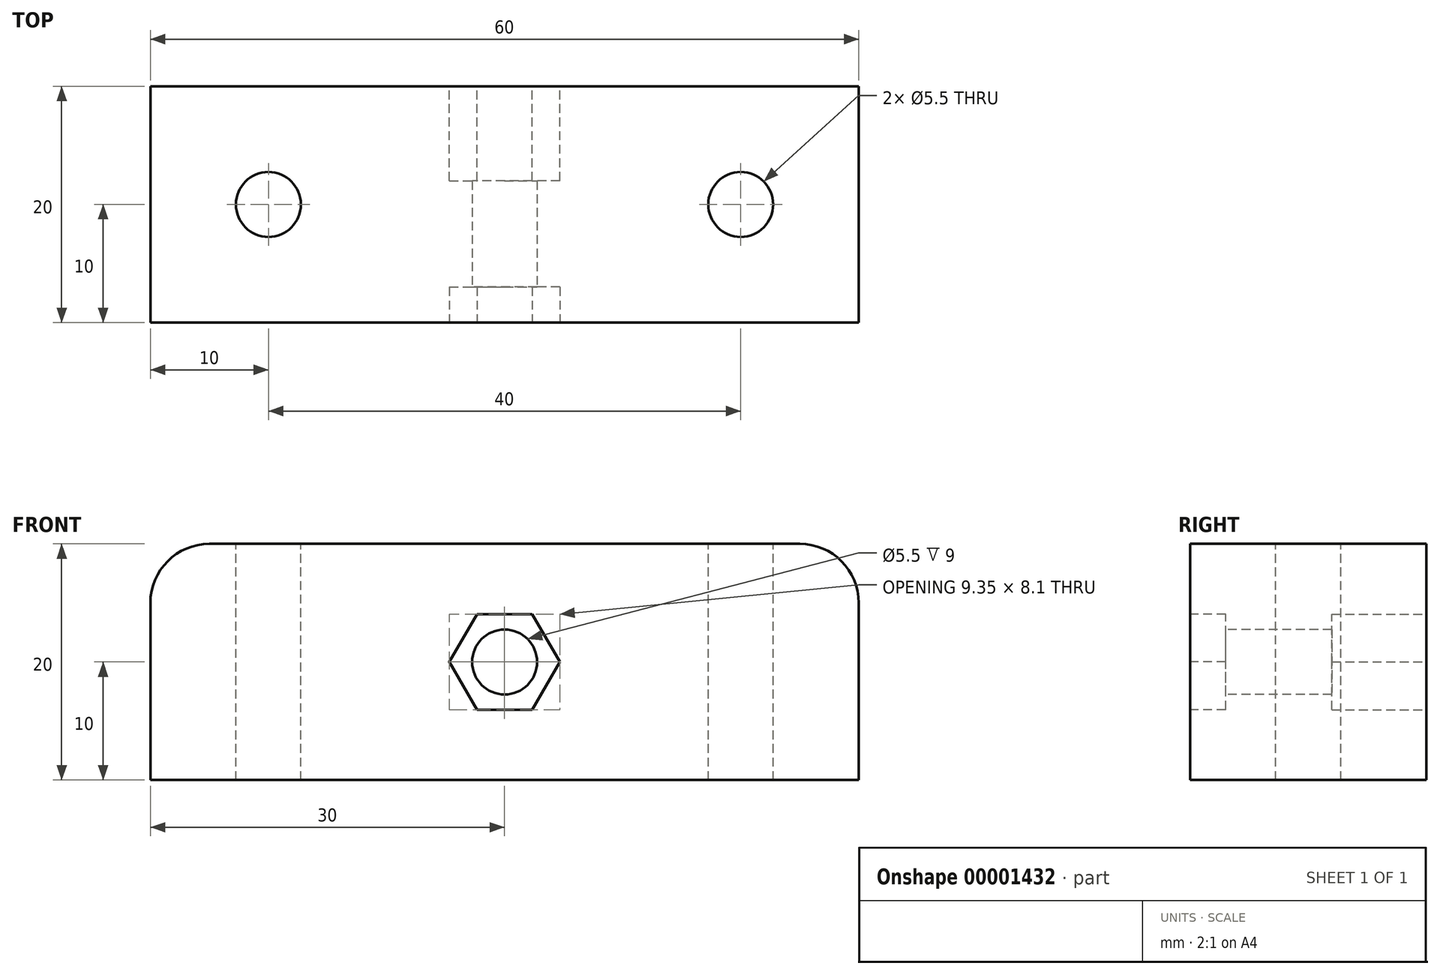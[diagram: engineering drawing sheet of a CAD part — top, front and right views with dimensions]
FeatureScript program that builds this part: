
annotation { "Feature Type Name" : "Feature", "Feature Type Description" : "" }
export const myFeature = defineFeature(function(context is Context, id is Id, definition is map)
    precondition{}
    {
        {
            var Q0;
            Q0=qCreatedBy(makeId("Top.planeOp"),FACE);
            var sketch = newSketch(context, id + "F0", { "sketchPlane" : qUnion([Q0])});
            skLineSegment(sketch, "E0.rect.bottom", {"start": v(30, 10) * mm, "end": v(-30, 10) * mm});
            skLineSegment(sketch, "E0.rect.top", {"start": v(30, -10) * mm, "end": v(-30, -10) * mm});
            skLineSegment(sketch, "E0.rect.left", {"start": v(30, 10) * mm, "end": v(30, -10) * mm});
            skLineSegment(sketch, "E0.rect.right", {"start": v(-30, 10) * mm, "end": v(-30, -10) * mm});
            skPoint(sketch, "E0.rect.middle", {"position": v(0, 0) * mm});
            skSolve(sketch);
        }
        {
            var Q0;
            Q0=makeQuery(id+"F0.imprint","IMPRINT",FACE,{"disambiguationData":[TD([[makeQuery(id+"F0.imprint","IMPRINT",EDGE,{"derivedFrom":sQuery(id+"F0.wireOp",EDGE,"E0.rect.bottom")}),1.0]])]});
            extrude(context, id + "F1", {"entities" : qUnion([Q0]), "depth" : 20 * mm});
        }
        {
            var Q0;
            Q0=makeQuery(id+"F1.opExtrude","SWEPT_FACE",FACE,{"disambiguationData":[OSD([sQuery(id+"F0.wireOp",EDGE,"E0.rect.top")])]});
            var sketch = newSketch(context, id + "F2", { "sketchPlane" : qUnion([Q0])});
            skLineSegment(sketch, "E1", {"start": v(0, 0) * mm, "end": v(0, 20) * mm, "construction": true});
            skCircle(sketch, "E2", {"center": v(0, 10) * mm, "radius": 2.75 * mm});
            skSolve(sketch);
        }
        {
            var Q0;
            Q0=makeQuery(id+"F2.imprint","IMPRINT",FACE,{"disambiguationData":[TD([[makeQuery(id+"F2.imprint","IMPRINT",EDGE,{"derivedFrom":sQuery(id+"F2.wireOp",EDGE,"E2")}),1.0]])]});
            extrude(context, id + "F3", {"entities" : qUnion([Q0]), "operationType" : NewBodyOperationType.REMOVE, "endBound" : BoundingType.THROUGH_ALL, "oppositeDirection" : true, "depth" : 25 * mm});
        }
        {
            var Q0;
            Q0=makeQuery(id+"F1.opExtrude","SWEPT_FACE",FACE,{"disambiguationData":[OSD([sQuery(id+"F0.wireOp",EDGE,"E0.rect.top")])]});
            var sketch = newSketch(context, id + "F4", { "sketchPlane" : qUnion([Q0])});
            skCircle(sketch, "E3.cCircle", {"center": v(0, 10) * mm, "radius": 4.05 * mm, "construction": true});
            skLineSegment(sketch, "E3.0", {"start": v(-2.34, 14.05) * mm, "end": v(2.34, 14.05) * mm});
            skLineSegment(sketch, "E3.1", {"start": v(2.34, 14.05) * mm, "end": v(4.68, 10) * mm});
            skLineSegment(sketch, "E3.2", {"start": v(4.68, 10) * mm, "end": v(2.34, 5.95) * mm});
            skLineSegment(sketch, "E3.3", {"start": v(2.34, 5.95) * mm, "end": v(-2.34, 5.95) * mm});
            skLineSegment(sketch, "E3.4", {"start": v(-2.34, 5.95) * mm, "end": v(-4.68, 10) * mm});
            skLineSegment(sketch, "E3.5", {"start": v(-4.68, 10) * mm, "end": v(-2.34, 14.05) * mm});
            skPoint(sketch, "E3.0.midPoint", {"position": v(0, 14.05) * mm});
            skSolve(sketch);
        }
        {
            var Q0;
            {var subQ0=makeQuery(id+"F4.imprint","IMPRINT",EDGE,{"derivedFrom":makeQuery(id+"F3.boolean.opBoolean","COPY",EDGE,{"derivedFrom":makeQuery(id+"F3.opExtrude","CAP_EDGE",EDGE,{"disambiguationData":[OSD([sQuery(id+"F2.wireOp",EDGE,"E2")])],"isStart":true})})});Q0=qUnion([makeQuery(id+"F4.imprint","IMPRINT",FACE,{"disambiguationData":[TD([[subQ0,1.0]])]}),makeQuery(id+"F4.imprint","IMPRINT",FACE,{"disambiguationData":[TD([[makeQuery(id+"F4.imprint","IMPRINT",EDGE,{"derivedFrom":sQuery(id+"F4.wireOp",EDGE,"E3.0")}),-1.0]])]})]);}
            extrude(context, id + "F5", {"entities" : qUnion([Q0]), "operationType" : NewBodyOperationType.REMOVE, "oppositeDirection" : true, "depth" : 3 * mm});
        }
        {
            var Q0;
            Q0=makeQuery(id+"F1.opExtrude","SWEPT_FACE",FACE,{"disambiguationData":[OSD([sQuery(id+"F0.wireOp",EDGE,"E0.rect.bottom")])]});
            var sketch = newSketch(context, id + "F6", { "sketchPlane" : qUnion([Q0])});
            skCircle(sketch, "E4.cCircle", {"center": v(0, 10) * mm, "radius": 4.05 * mm, "construction": true});
            skLineSegment(sketch, "E4.0", {"start": v(-2.34, 14.05) * mm, "end": v(2.34, 14.05) * mm});
            skLineSegment(sketch, "E4.1", {"start": v(2.34, 14.05) * mm, "end": v(4.68, 10) * mm});
            skLineSegment(sketch, "E4.2", {"start": v(4.68, 10) * mm, "end": v(2.34, 5.95) * mm});
            skLineSegment(sketch, "E4.3", {"start": v(2.34, 5.95) * mm, "end": v(-2.34, 5.95) * mm});
            skLineSegment(sketch, "E4.4", {"start": v(-2.34, 5.95) * mm, "end": v(-4.68, 10) * mm});
            skLineSegment(sketch, "E4.5", {"start": v(-4.68, 10) * mm, "end": v(-2.34, 14.05) * mm});
            skPoint(sketch, "E4.0.midPoint", {"position": v(0, 14.05) * mm});
            skSolve(sketch);
        }
        {
            var Q0;
            {var subQ0=makeQuery(id+"F6.imprint","IMPRINT",EDGE,{"derivedFrom":makeQuery(id+"F3.boolean.opBoolean","INTERSECT",EDGE,{"derivedFrom":[makeQuery(id+"F1.opExtrude","SWEPT_FACE",FACE,{"disambiguationData":[OSD([sQuery(id+"F0.wireOp",EDGE,"E0.rect.bottom")])]}),makeQuery(id+"F3.opExtrude","SWEPT_FACE",FACE,{"disambiguationData":[OSD([sQuery(id+"F2.wireOp",EDGE,"E2")])]})]})});Q0=qUnion([makeQuery(id+"F6.imprint","IMPRINT",FACE,{"disambiguationData":[TD([[subQ0,-1.0]])]}),makeQuery(id+"F6.imprint","IMPRINT",FACE,{"disambiguationData":[TD([[makeQuery(id+"F6.imprint","IMPRINT",EDGE,{"derivedFrom":sQuery(id+"F6.wireOp",EDGE,"E4.0")}),-1.0]])]})]);}
            extrude(context, id + "F7", {"entities" : qUnion([Q0]), "operationType" : NewBodyOperationType.REMOVE, "oppositeDirection" : true, "depth" : 8 * mm});
        }
        {
            var Q0;
            Q0=makeQuery(id+"F1.opExtrude","CAP_FACE",FACE,{"disambiguationData":[OSD([sQuery(id+"F0.wireOp",EDGE,"E0.rect.bottom"),sQuery(id+"F0.wireOp",EDGE,"E0.rect.top"),sQuery(id+"F0.wireOp",EDGE,"E0.rect.left"),sQuery(id+"F0.wireOp",EDGE,"E0.rect.right")])],"isStart":false});
            var sketch = newSketch(context, id + "F8", { "sketchPlane" : qUnion([Q0])});
            skLineSegment(sketch, "E5", {"start": v(30, 0) * mm, "end": v(20, 0) * mm, "construction": true});
            skLineSegment(sketch, "E6", {"start": v(20, 0) * mm, "end": v(-20, 0) * mm, "construction": true});
            skLineSegment(sketch, "E7", {"start": v(-20, 0) * mm, "end": v(-30, 0) * mm, "construction": true});
            skCircle(sketch, "E8", {"center": v(20, 0) * mm, "radius": 2.75 * mm});
            skCircle(sketch, "E9", {"center": v(-20, 0) * mm, "radius": 2.75 * mm});
            skSolve(sketch);
        }
        {
            var Q0;
            {Q0=qUnion([makeQuery(id+"F8.imprint","IMPRINT",FACE,{"disambiguationData":[TD([[makeQuery(id+"F8.imprint","IMPRINT",EDGE,{"derivedFrom":sQuery(id+"F8.wireOp",EDGE,"E8")}),1.0]])]}),makeQuery(id+"F8.imprint","IMPRINT",FACE,{"disambiguationData":[TD([[makeQuery(id+"F8.imprint","IMPRINT",EDGE,{"derivedFrom":sQuery(id+"F8.wireOp",EDGE,"E9")}),1.0]])]})]);}
            extrude(context, id + "F9", {"entities" : qUnion([Q0]), "operationType" : NewBodyOperationType.REMOVE, "endBound" : BoundingType.THROUGH_ALL, "oppositeDirection" : true, "depth" : 25 * mm});
        }
        {
            var Q0;
            Q0=makeQuery(id+"F1.opExtrude","CAP_EDGE",EDGE,{"disambiguationData":[OSD([sQuery(id+"F0.wireOp",EDGE,"E0.rect.right")])],"isStart":false});
            var Q1;
            Q1=makeQuery(id+"F1.opExtrude","CAP_EDGE",EDGE,{"disambiguationData":[OSD([sQuery(id+"F0.wireOp",EDGE,"E0.rect.left")])],"isStart":false});
            fillet(context, id + "F10", {"entities" : qUnion([Q0, Q1]), "radius" : 5 * mm, "tangentPropagation" : true, "allowEdgeOverflow" : false});
        }
    });
